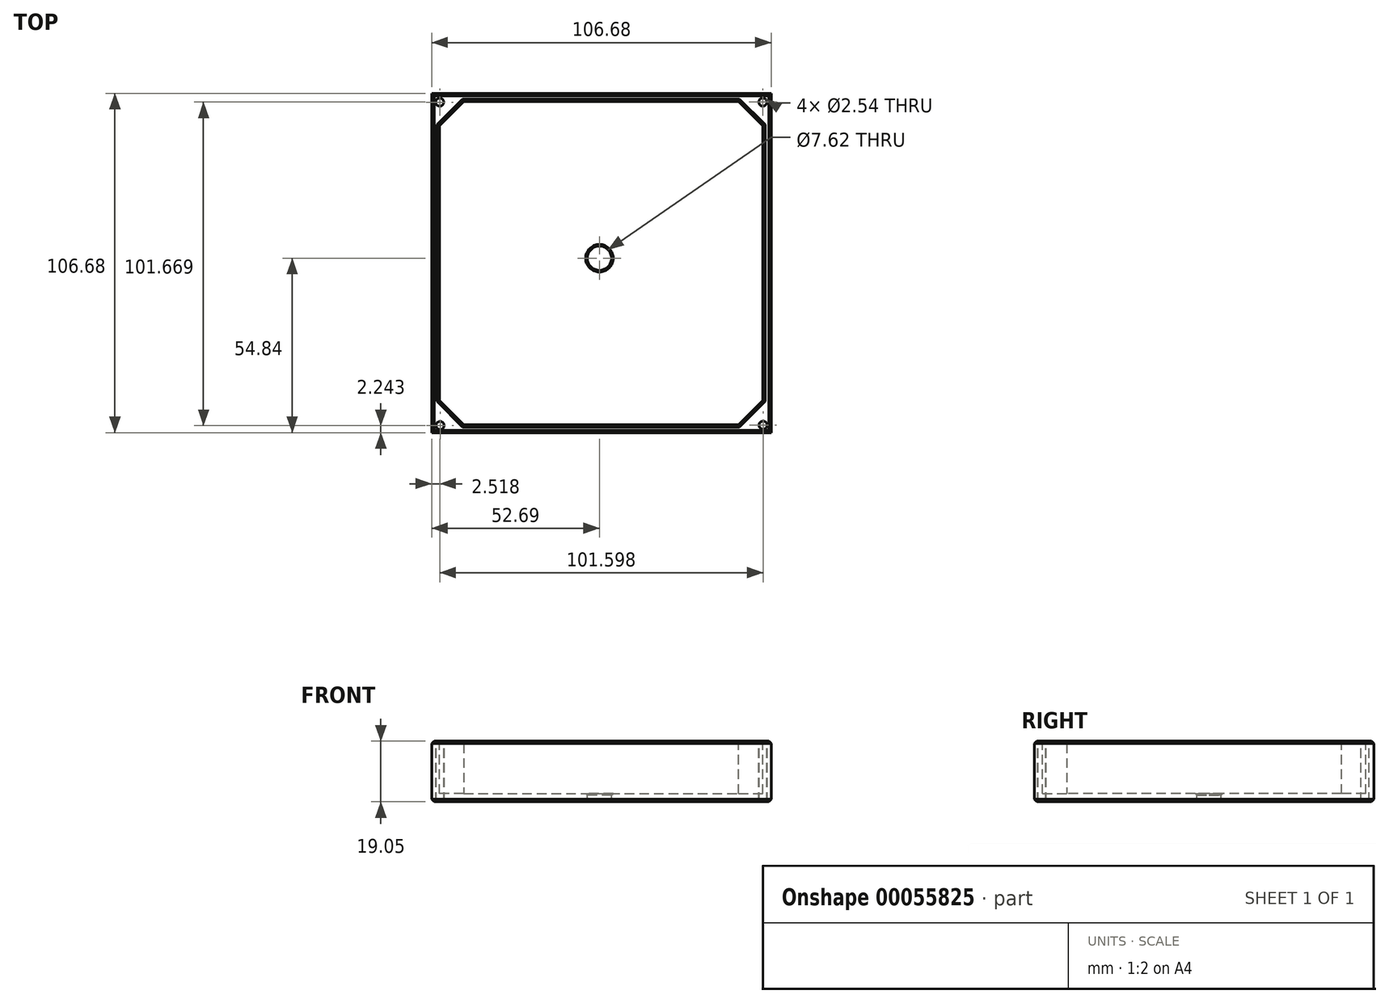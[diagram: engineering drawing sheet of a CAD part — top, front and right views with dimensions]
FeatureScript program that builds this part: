
annotation { "Feature Type Name" : "Feature", "Feature Type Description" : "" }
export const myFeature = defineFeature(function(context is Context, id is Id, definition is map)
    precondition{}
    {
        {
            var Q0;
            Q0=qCreatedBy(makeId("Top.planeOp"),FACE);
            var sketch = newSketch(context, id + "F0", { "sketchPlane" : qUnion([Q0])});
            skLineSegment(sketch, "E0.bottom", {"start": v(-50.26, 49.27) * mm, "end": v(51.34, 49.27) * mm});
            skLineSegment(sketch, "E0.top", {"start": v(-50.26, -52.33) * mm, "end": v(51.34, -52.33) * mm});
            skLineSegment(sketch, "E0.left", {"start": v(-50.26, 49.27) * mm, "end": v(-50.26, -52.33) * mm});
            skLineSegment(sketch, "E0.right", {"start": v(51.34, 49.27) * mm, "end": v(51.34, -52.33) * mm});
            skLineSegment(sketch, "E1.bottom", {"start": v(-52.7, 51.84) * mm, "end": v(53.99, 51.84) * mm});
            skLineSegment(sketch, "E1.top", {"start": v(-52.7, -54.84) * mm, "end": v(53.99, -54.84) * mm});
            skLineSegment(sketch, "E1.left", {"start": v(-52.7, 51.84) * mm, "end": v(-52.7, -54.84) * mm});
            skLineSegment(sketch, "E1.right", {"start": v(53.99, 51.84) * mm, "end": v(53.99, -54.84) * mm});
            skSolve(sketch);
        }
        {
            var Q0;
            Q0 = qSketchRegion(id + "F0", true);
            extrude(context, id + "F1", {"entities" : qUnion([Q0]), "depth" : 19.05 * mm});
        }
        {
            var Q0;
            Q0=qCreatedBy(makeId("Top.planeOp"),FACE);
            var sketch = newSketch(context, id + "F2", { "sketchPlane" : qUnion([Q0])});
            skLineSegment(sketch, "E2.bottom", {"start": v(-51.72, 50.39) * mm, "end": v(52.94, 50.39) * mm});
            skLineSegment(sketch, "E2.top", {"start": v(-51.72, -54.03) * mm, "end": v(52.94, -54.03) * mm});
            skLineSegment(sketch, "E2.left", {"start": v(-51.72, 50.39) * mm, "end": v(-51.72, -54.03) * mm});
            skLineSegment(sketch, "E2.right", {"start": v(52.94, 50.39) * mm, "end": v(52.94, -54.03) * mm});
            skSolve(sketch);
        }
        {
            var Q0;
            Q0 = qSketchRegion(id + "F2", true);
            extrude(context, id + "F3", {"entities" : qUnion([Q0]), "operationType" : NewBodyOperationType.ADD, "depth" : 2.54 * mm});
        }
        {
            var Q0;
            Q0=qCreatedBy(makeId("Top.planeOp"),FACE);
            var sketch = newSketch(context, id + "F4", { "sketchPlane" : qUnion([Q0])});
            skCircle(sketch, "E3", {"center": v(0, 0) * mm, "radius": 3.8 * mm});
            skSolve(sketch);
        }
        {
            var Q0;
            Q0 = qSketchRegion(id + "F4", true);
            extrude(context, id + "F5", {"entities" : qUnion([Q0]), "operationType" : NewBodyOperationType.REMOVE, "endBound" : BoundingType.SYMMETRIC, "oppositeDirection" : true, "depth" : 25.4 * mm});
        }
        {
            var Q0;
            Q0=makeQuery(id+"F1.opExtrude","SWEPT_EDGE",EDGE,{"disambiguationData":[OSD([sQuery(id+"F0.wireOp",EDGE,"E0.bottom"),sQuery(id+"F0.wireOp",EDGE,"E0.left")])]});
            var Q1;
            Q1=makeQuery(id+"F1.opExtrude","SWEPT_EDGE",EDGE,{"disambiguationData":[OSD([sQuery(id+"F0.wireOp",EDGE,"E0.bottom"),sQuery(id+"F0.wireOp",EDGE,"E0.right")])]});
            var Q2;
            Q2=makeQuery(id+"F1.opExtrude","SWEPT_EDGE",EDGE,{"disambiguationData":[OSD([sQuery(id+"F0.wireOp",EDGE,"E0.top"),sQuery(id+"F0.wireOp",EDGE,"E0.right")])]});
            var Q3;
            Q3=makeQuery(id+"F1.opExtrude","SWEPT_EDGE",EDGE,{"disambiguationData":[OSD([sQuery(id+"F0.wireOp",EDGE,"E0.top"),sQuery(id+"F0.wireOp",EDGE,"E0.left")])]});
            chamfer(context, id + "F6", {"entities" : qUnion([Q0, Q1, Q2, Q3]), "width" : 7.62 * mm, "tangentPropagation" : true});
        }
        {
            var Q0;
            Q0=qCreatedBy(makeId("Top.planeOp"),FACE);
            var sketch = newSketch(context, id + "F7", { "sketchPlane" : qUnion([Q0])});
            skCircle(sketch, "E4", {"center": v(-50.17, 49.06) * mm, "radius": 1.27 * mm});
            skCircle(sketch, "E5", {"center": v(51.35, 49.07) * mm, "radius": 1.27 * mm});
            skCircle(sketch, "E6", {"center": v(51.43, -52.49) * mm, "radius": 1.27 * mm});
            skCircle(sketch, "E7", {"center": v(-50.06, -52.6) * mm, "radius": 1.27 * mm});
            skSolve(sketch);
        }
        {
            var Q0;
            Q0 = qSketchRegion(id + "F7", true);
            extrude(context, id + "F8", {"entities" : qUnion([Q0]), "operationType" : NewBodyOperationType.REMOVE, "endBound" : BoundingType.SYMMETRIC, "oppositeDirection" : true, "depth" : 76.2 * mm});
        }
        {
            var Q0;
            Q0=makeQuery(id+"F5.boolean.opBoolean","INTERSECT",EDGE,{"derivedFrom":[makeQuery(id+"F3.opExtrude","CAP_FACE",FACE,{"disambiguationData":[OSD([sQuery(id+"F2.wireOp",EDGE,"E2.bottom"),sQuery(id+"F2.wireOp",EDGE,"E2.top"),sQuery(id+"F2.wireOp",EDGE,"E2.left"),sQuery(id+"F2.wireOp",EDGE,"E2.right")])],"isStart":false}),makeQuery(id+"F5.opExtrude","SWEPT_FACE",FACE,{"disambiguationData":[OSD([sQuery(id+"F4.wireOp",EDGE,"E3")])]})]});
            var Q1;
            Q1=makeQuery(id+"F5.boolean.opBoolean","INTERSECT",EDGE,{"derivedFrom":[makeQuery(id+"F3.boolean.opBoolean","MERGE",FACE,{"derivedFrom":[makeQuery(id+"F1.opExtrude","CAP_FACE",FACE,{"disambiguationData":[OSD([sQuery(id+"F0.wireOp",EDGE,"E0.bottom"),sQuery(id+"F0.wireOp",EDGE,"E0.top"),sQuery(id+"F0.wireOp",EDGE,"E0.left"),sQuery(id+"F0.wireOp",EDGE,"E0.right"),sQuery(id+"F0.wireOp",EDGE,"E1.bottom"),sQuery(id+"F0.wireOp",EDGE,"E1.top"),sQuery(id+"F0.wireOp",EDGE,"E1.left"),sQuery(id+"F0.wireOp",EDGE,"E1.right")])],"isStart":true}),makeQuery(id+"F3.opExtrude","CAP_FACE",FACE,{"disambiguationData":[OSD([sQuery(id+"F2.wireOp",EDGE,"E2.bottom"),sQuery(id+"F2.wireOp",EDGE,"E2.top"),sQuery(id+"F2.wireOp",EDGE,"E2.left"),sQuery(id+"F2.wireOp",EDGE,"E2.right")])],"isStart":true})]}),makeQuery(id+"F5.opExtrude","SWEPT_FACE",FACE,{"disambiguationData":[OSD([sQuery(id+"F4.wireOp",EDGE,"E3")])]})]});
            chamfer(context, id + "F9", {"entities" : qUnion([Q0, Q1]), "width" : 0.5 * mm, "tangentPropagation" : true});
        }
        {
            var Q0;
            Q0=makeQuery(id+"F1.opExtrude","CAP_EDGE",EDGE,{"disambiguationData":[OSD([sQuery(id+"F0.wireOp",EDGE,"E1.top")])],"isStart":false});
            var Q1;
            Q1=makeQuery(id+"F1.opExtrude","CAP_EDGE",EDGE,{"disambiguationData":[OSD([sQuery(id+"F0.wireOp",EDGE,"E1.left")])],"isStart":false});
            var Q2;
            Q2=makeQuery(id+"F1.opExtrude","CAP_EDGE",EDGE,{"disambiguationData":[OSD([sQuery(id+"F0.wireOp",EDGE,"E1.right")])],"isStart":false});
            var Q3;
            Q3=makeQuery(id+"F1.opExtrude","CAP_EDGE",EDGE,{"disambiguationData":[OSD([sQuery(id+"F0.wireOp",EDGE,"E1.bottom")])],"isStart":false});
            var Q4;
            Q4=makeQuery(id+"F1.opExtrude","CAP_EDGE",EDGE,{"disambiguationData":[OSD([sQuery(id+"F0.wireOp",EDGE,"E0.right")])],"isStart":false});
            var Q5;
            {var subQ0=sQuery(id+"F0.wireOp",EDGE,"E0.right");var subQ1=sQuery(id+"F0.wireOp",EDGE,"E0.top");Q5=makeQuery(id+"F6.opChamfer","BLEND_EDGE",EDGE,{"blendedFrom":[makeQuery(id+"F1.opExtrude","SWEPT_EDGE",EDGE,{"disambiguationData":[OSD([subQ1,subQ0])]}),makeQuery(id+"F1.opExtrude","CAP_FACE",FACE,{"disambiguationData":[OSD([sQuery(id+"F0.wireOp",EDGE,"E0.bottom"),subQ1,sQuery(id+"F0.wireOp",EDGE,"E0.left"),subQ0,sQuery(id+"F0.wireOp",EDGE,"E1.bottom"),sQuery(id+"F0.wireOp",EDGE,"E1.top"),sQuery(id+"F0.wireOp",EDGE,"E1.left"),sQuery(id+"F0.wireOp",EDGE,"E1.right")])],"isStart":false})],"blendedInto":[makeQuery(id+"F1.opExtrude","CAP_FACE",FACE,{"disambiguationData":[OSD([sQuery(id+"F0.wireOp",EDGE,"E0.bottom"),subQ1,sQuery(id+"F0.wireOp",EDGE,"E0.left"),subQ0,sQuery(id+"F0.wireOp",EDGE,"E1.bottom"),sQuery(id+"F0.wireOp",EDGE,"E1.top"),sQuery(id+"F0.wireOp",EDGE,"E1.left"),sQuery(id+"F0.wireOp",EDGE,"E1.right")])],"isStart":false})]});}
            var Q6;
            Q6=makeQuery(id+"F1.opExtrude","CAP_EDGE",EDGE,{"disambiguationData":[OSD([sQuery(id+"F0.wireOp",EDGE,"E0.top")])],"isStart":false});
            var Q7;
            {var subQ0=sQuery(id+"F0.wireOp",EDGE,"E0.right");var subQ1=sQuery(id+"F0.wireOp",EDGE,"E0.bottom");Q7=makeQuery(id+"F6.opChamfer","BLEND_EDGE",EDGE,{"blendedFrom":[makeQuery(id+"F1.opExtrude","SWEPT_EDGE",EDGE,{"disambiguationData":[OSD([subQ1,subQ0])]}),makeQuery(id+"F1.opExtrude","CAP_FACE",FACE,{"disambiguationData":[OSD([subQ1,sQuery(id+"F0.wireOp",EDGE,"E0.top"),sQuery(id+"F0.wireOp",EDGE,"E0.left"),subQ0,sQuery(id+"F0.wireOp",EDGE,"E1.bottom"),sQuery(id+"F0.wireOp",EDGE,"E1.top"),sQuery(id+"F0.wireOp",EDGE,"E1.left"),sQuery(id+"F0.wireOp",EDGE,"E1.right")])],"isStart":false})],"blendedInto":[makeQuery(id+"F1.opExtrude","CAP_FACE",FACE,{"disambiguationData":[OSD([subQ1,sQuery(id+"F0.wireOp",EDGE,"E0.top"),sQuery(id+"F0.wireOp",EDGE,"E0.left"),subQ0,sQuery(id+"F0.wireOp",EDGE,"E1.bottom"),sQuery(id+"F0.wireOp",EDGE,"E1.top"),sQuery(id+"F0.wireOp",EDGE,"E1.left"),sQuery(id+"F0.wireOp",EDGE,"E1.right")])],"isStart":false})]});}
            var Q8;
            Q8=makeQuery(id+"F1.opExtrude","CAP_EDGE",EDGE,{"disambiguationData":[OSD([sQuery(id+"F0.wireOp",EDGE,"E0.bottom")])],"isStart":false});
            var Q9;
            {var subQ0=sQuery(id+"F0.wireOp",EDGE,"E0.left");var subQ1=sQuery(id+"F0.wireOp",EDGE,"E0.bottom");Q9=makeQuery(id+"F6.opChamfer","BLEND_EDGE",EDGE,{"blendedFrom":[makeQuery(id+"F1.opExtrude","SWEPT_EDGE",EDGE,{"disambiguationData":[OSD([subQ1,subQ0])]}),makeQuery(id+"F1.opExtrude","CAP_FACE",FACE,{"disambiguationData":[OSD([subQ1,sQuery(id+"F0.wireOp",EDGE,"E0.top"),subQ0,sQuery(id+"F0.wireOp",EDGE,"E0.right"),sQuery(id+"F0.wireOp",EDGE,"E1.bottom"),sQuery(id+"F0.wireOp",EDGE,"E1.top"),sQuery(id+"F0.wireOp",EDGE,"E1.left"),sQuery(id+"F0.wireOp",EDGE,"E1.right")])],"isStart":false})],"blendedInto":[makeQuery(id+"F1.opExtrude","CAP_FACE",FACE,{"disambiguationData":[OSD([subQ1,sQuery(id+"F0.wireOp",EDGE,"E0.top"),subQ0,sQuery(id+"F0.wireOp",EDGE,"E0.right"),sQuery(id+"F0.wireOp",EDGE,"E1.bottom"),sQuery(id+"F0.wireOp",EDGE,"E1.top"),sQuery(id+"F0.wireOp",EDGE,"E1.left"),sQuery(id+"F0.wireOp",EDGE,"E1.right")])],"isStart":false})]});}
            var Q10;
            Q10=makeQuery(id+"F1.opExtrude","CAP_EDGE",EDGE,{"disambiguationData":[OSD([sQuery(id+"F0.wireOp",EDGE,"E0.left")])],"isStart":false});
            var Q11;
            {var subQ0=sQuery(id+"F0.wireOp",EDGE,"E0.left");var subQ1=sQuery(id+"F0.wireOp",EDGE,"E0.top");Q11=makeQuery(id+"F6.opChamfer","BLEND_EDGE",EDGE,{"blendedFrom":[makeQuery(id+"F1.opExtrude","SWEPT_EDGE",EDGE,{"disambiguationData":[OSD([subQ1,subQ0])]}),makeQuery(id+"F1.opExtrude","CAP_FACE",FACE,{"disambiguationData":[OSD([sQuery(id+"F0.wireOp",EDGE,"E0.bottom"),subQ1,subQ0,sQuery(id+"F0.wireOp",EDGE,"E0.right"),sQuery(id+"F0.wireOp",EDGE,"E1.bottom"),sQuery(id+"F0.wireOp",EDGE,"E1.top"),sQuery(id+"F0.wireOp",EDGE,"E1.left"),sQuery(id+"F0.wireOp",EDGE,"E1.right")])],"isStart":false})],"blendedInto":[makeQuery(id+"F1.opExtrude","CAP_FACE",FACE,{"disambiguationData":[OSD([sQuery(id+"F0.wireOp",EDGE,"E0.bottom"),subQ1,subQ0,sQuery(id+"F0.wireOp",EDGE,"E0.right"),sQuery(id+"F0.wireOp",EDGE,"E1.bottom"),sQuery(id+"F0.wireOp",EDGE,"E1.top"),sQuery(id+"F0.wireOp",EDGE,"E1.left"),sQuery(id+"F0.wireOp",EDGE,"E1.right")])],"isStart":false})]});}
            chamfer(context, id + "F10", {"entities" : qUnion([Q0, Q1, Q2, Q3, Q4, Q5, Q6, Q7, Q8, Q9, Q10, Q11]), "width" : 0.76 * mm, "tangentPropagation" : true});
        }
        {
            var Q0;
            Q0=makeQuery(id+"F1.opExtrude","CAP_EDGE",EDGE,{"disambiguationData":[OSD([sQuery(id+"F0.wireOp",EDGE,"E1.left")])],"isStart":true});
            var Q1;
            Q1=makeQuery(id+"F1.opExtrude","CAP_EDGE",EDGE,{"disambiguationData":[OSD([sQuery(id+"F0.wireOp",EDGE,"E1.bottom")])],"isStart":true});
            var Q2;
            Q2=makeQuery(id+"F1.opExtrude","CAP_EDGE",EDGE,{"disambiguationData":[OSD([sQuery(id+"F0.wireOp",EDGE,"E1.top")])],"isStart":true});
            var Q3;
            Q3=makeQuery(id+"F1.opExtrude","CAP_EDGE",EDGE,{"disambiguationData":[OSD([sQuery(id+"F0.wireOp",EDGE,"E1.right")])],"isStart":true});
            chamfer(context, id + "F11", {"entities" : qUnion([Q0, Q1, Q2, Q3]), "width" : 0.76 * mm, "tangentPropagation" : true});
        }
    });
